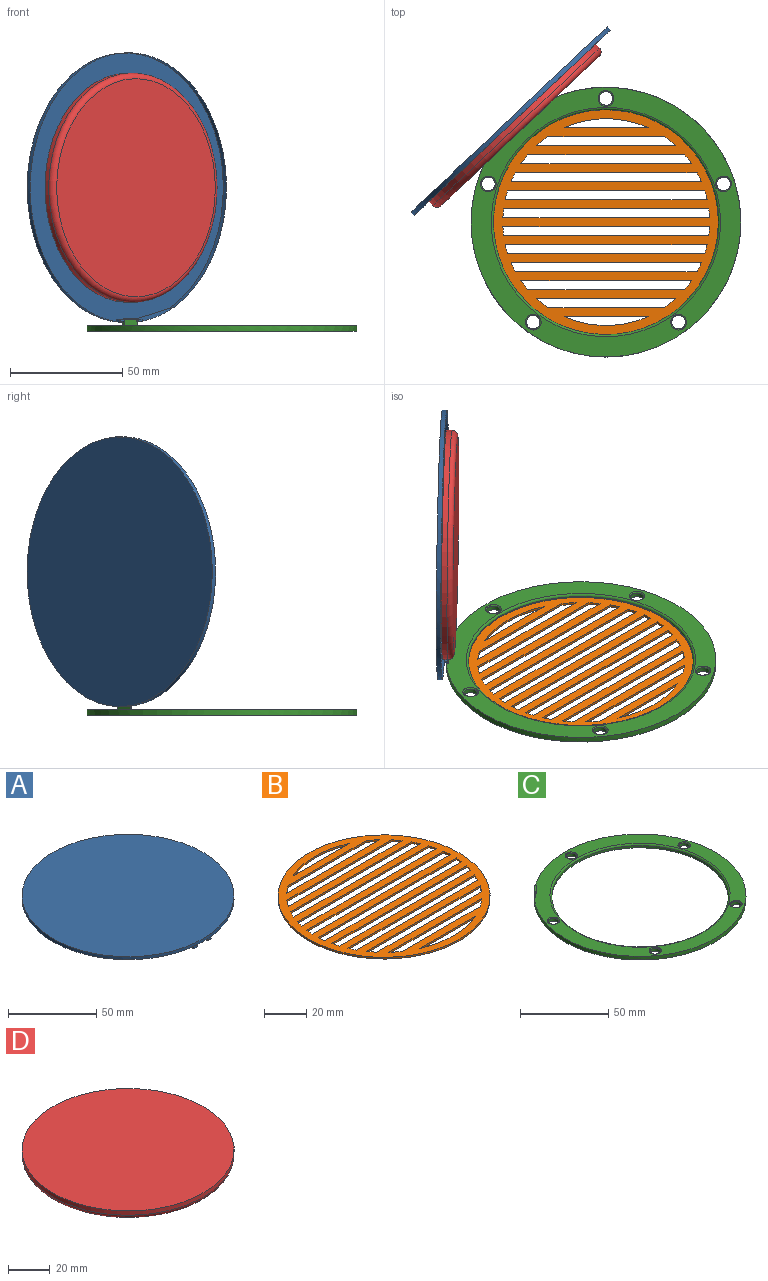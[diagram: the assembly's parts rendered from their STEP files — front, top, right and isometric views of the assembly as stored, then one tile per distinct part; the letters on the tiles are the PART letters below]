
ASSEMBLY  parts=4 mates=3
PART A: 21 faces, bbox 120x120x4 mm
  f0: plane 3x1.5mm, normal (0,1,0), area 4.5mm2, adj f4,f8,f10,f18
  f1: plane 3x1.5mm, normal (0,-1,0), area 4.5mm2, adj f4,f8,f10,f18
  f2: cylinder r=60mm len=120mm, axis (0,0,-1), area 754mm2, adj f3,f4
  f3: plane 120x120mm, normal (0,0,1), area 11309.7mm2, adj f2
  f4: plane 120x120mm, normal (0,0,-1), area 11303.7mm2, adj f0,f1,f2,f5,f6,f7,f8,f9
  f5: plane 3x1.5mm, normal (0,-1,0), area 4.5mm2, adj f4,f6,f9,f15
  f6: plane 1.5x1mm, normal (-1,0,0), area 1.5mm2, adj f4,f5,f7,f17
  f7: plane 3x1.5mm, normal (0,1,0), area 4.5mm2, adj f4,f6,f9,f15
  f8: plane 1.5x1mm, normal (1,0,0), area 1.5mm2, adj f0,f1,f4,f20
  f9: plane 1.5x1mm, normal (1,0,0), area 1.1mm2, adj f4,f5,f7,f13,f16
  f10: plane 1.5x1mm, normal (-1,0,0), area 1.1mm2, adj f0,f1,f4,f11,f19
  f11: cylinder r=0.35mm len=0.7mm, axis (1,0,0), area 0.6mm2, adj f10,f12,f19
  f12: plane 0.7x0.7mm, normal (-1,0,0), area 0.4mm2, adj f11
  f13: cylinder r=0.35mm len=0.7mm, axis (1,0,0), area 0.6mm2, adj f9,f14,f16
  f14: plane 0.7x0.7mm, normal (1,0,0), area 0.4mm2, adj f13
  f15: cylinder r=0.5mm len=3mm, axis (1,0,0), area 4.1mm2, adj f5,f7,f16,f17
  f16: cylinder r=0.5mm len=1mm, axis (0,-1,0), area 0.5mm2, adj f9,f13,f15
  f17: cylinder r=0.5mm len=1mm, axis (0,-1,0), area 0.5mm2, adj f6,f15
  f18: cylinder r=0.5mm len=3mm, axis (-1,0,0), area 4.1mm2, adj f0,f1,f19,f20
  f19: cylinder r=0.5mm len=1mm, axis (0,1,0), area 0.5mm2, adj f10,f11,f18
  f20: cylinder r=0.5mm len=1mm, axis (0,1,0), area 0.5mm2, adj f8,f18
PART B: 47 faces, bbox 100x100x1 mm
  f0: cylinder r=46mm len=37.52mm, axis (0,0,1), area 38.7mm2, adj f11,f12,f24
  f1: cylinder r=46mm len=5.06mm, axis (0,0,1), area 6.5mm2, adj f11,f12,f21,f23
  f2: cylinder r=46mm len=4mm, axis (0,0,1), area 5mm2, adj f11,f12,f19,f22
  f3: cylinder r=46mm len=5.06mm, axis (0,0,1), area 6.5mm2, adj f11,f12,f21,f23
  f4: cylinder r=46mm len=4mm, axis (0,0,1), area 4.4mm2, adj f11,f12,f17,f20
  f5: cylinder r=46mm len=4mm, axis (0,0,1), area 5mm2, adj f11,f12,f19,f22
  f6: cylinder r=46mm len=4mm, axis (0,0,1), area 4.1mm2, adj f11,f12,f15,f18
  f7: cylinder r=46mm len=4mm, axis (0,0,1), area 4.4mm2, adj f11,f12,f17,f20
  f8: cylinder r=46mm len=4mm, axis (0,0,1), area 4mm2, adj f11,f12,f14,f16
  f9: cylinder r=46mm len=4mm, axis (0,0,1), area 4.1mm2, adj f11,f12,f15,f18
  f10: cylinder r=50mm len=100mm, axis (0,0,-1), area 314.2mm2, adj f11,f12
  f11: plane 100x100mm, normal (0,0,1), area 4505.7mm2, adj f0,f1,f2,f3,f4,f5,f6,f7
  f12: plane 100x100mm, normal (0,0,-1), area 4505.7mm2, adj f0,f1,f2,f3,f4,f5,f6,f7
  f13: cylinder r=46mm len=4mm, axis (0,0,1), area 4mm2, adj f11,f12,f14,f16
  f14: plane 91.91x1mm, normal (0,1,0), area 91.9mm2, adj f8,f11,f12,f13
  f15: plane 89.8x1mm, normal (0,1,0), area 89.8mm2, adj f6,f9,f11,f12
  f16: plane 91.21x1mm, normal (0,-1,0), area 91.2mm2, adj f8,f11,f12,f13
  f17: plane 84.66x1mm, normal (0,1,0), area 84.7mm2, adj f4,f7,f11,f12
  f18: plane 87.64x1mm, normal (0,-1,0), area 87.6mm2, adj f6,f9,f11,f12
  f19: plane 75.89x1mm, normal (0,1,0), area 75.9mm2, adj f2,f5,f11,f12
  f20: plane 80.8x1mm, normal (0,-1,0), area 80.8mm2, adj f4,f7,f11,f12
  f21: plane 61.97x1mm, normal (0,1,0), area 62mm2, adj f1,f3,f11,f12
  f22: plane 69.74x1mm, normal (0,-1,0), area 69.7mm2, adj f2,f5,f11,f12
  f23: plane 51.85x1mm, normal (0,-1,0), area 51.8mm2, adj f1,f3,f11,f12
  f24: plane 37.52x1mm, normal (0,1,0), area 37.5mm2, adj f0,f11,f12
  f25: cylinder r=46mm len=37.52mm, axis (0,0,1), area 38.7mm2, adj f11,f12,f46
  f26: cylinder r=46mm len=5.06mm, axis (0,0,1), area 6.5mm2, adj f11,f12,f43,f45
  f27: cylinder r=46mm len=4mm, axis (0,0,1), area 5mm2, adj f11,f12,f41,f44
  f28: cylinder r=46mm len=5.06mm, axis (0,0,1), area 6.5mm2, adj f11,f12,f43,f45
  f29: cylinder r=46mm len=4mm, axis (0,0,1), area 4.4mm2, adj f11,f12,f39,f42
  f30: cylinder r=46mm len=4mm, axis (0,0,1), area 5mm2, adj f11,f12,f41,f44
  f31: cylinder r=46mm len=4mm, axis (0,0,1), area 4.1mm2, adj f11,f12,f37,f40
  f32: cylinder r=46mm len=4mm, axis (0,0,1), area 4.4mm2, adj f11,f12,f39,f42
  f33: cylinder r=46mm len=4mm, axis (0,0,1), area 4mm2, adj f11,f12,f36,f38
  f34: cylinder r=46mm len=4mm, axis (0,0,1), area 4.1mm2, adj f11,f12,f37,f40
  f35: cylinder r=46mm len=4mm, axis (0,0,1), area 4mm2, adj f11,f12,f36,f38
  f36: plane 91.91x1mm, normal (0,-1,0), area 91.9mm2, adj f11,f12,f33,f35
  f37: plane 89.8x1mm, normal (0,-1,0), area 89.8mm2, adj f11,f12,f31,f34
  f38: plane 91.21x1mm, normal (0,1,0), area 91.2mm2, adj f11,f12,f33,f35
  f39: plane 84.66x1mm, normal (0,-1,0), area 84.7mm2, adj f11,f12,f29,f32
  f40: plane 87.64x1mm, normal (0,1,0), area 87.6mm2, adj f11,f12,f31,f34
  f41: plane 75.89x1mm, normal (0,-1,0), area 75.9mm2, adj f11,f12,f27,f30
  f42: plane 80.8x1mm, normal (0,1,0), area 80.8mm2, adj f11,f12,f29,f32
  f43: plane 61.97x1mm, normal (0,-1,0), area 62mm2, adj f11,f12,f26,f28
  f44: plane 69.74x1mm, normal (0,1,0), area 69.7mm2, adj f11,f12,f27,f30
  f45: plane 51.85x1mm, normal (0,1,0), area 51.8mm2, adj f11,f12,f26,f28
  f46: plane 37.52x1mm, normal (0,-1,0), area 37.5mm2, adj f11,f12,f25
PART C: 22 faces, bbox 120x120x5.5 mm
  f0: plane 5.82x5.49mm, normal (0,0,1), area 0.7mm2, adj f2,f10
  f1: plane 120x120mm, normal (0,0,1), area 2937.3mm2, adj f2,f11,f12,f13,f15,f16,f17,f18
  f2: cylinder r=60mm len=120mm, axis (0,0,-1), area 942.5mm2, adj f0,f1,f3
  f3: plane 120x120mm, normal (0,0,-1), area 3314.4mm2, adj f2,f4,f5,f6,f7,f8,f9
  f4: cylinder r=50mm len=100mm, axis (0,0,1), area 471.2mm2, adj f3,f15
  f5: cylinder r=3mm len=6mm, axis (0,0,1), area 37.7mm2, adj f3,f20
  f6: cylinder r=3mm len=6mm, axis (0,0,1), area 37.7mm2, adj f3,f19
  f7: cylinder r=3mm len=6mm, axis (0,0,1), area 37.7mm2, adj f3,f18
  f8: cylinder r=3mm len=6mm, axis (0,0,1), area 37.7mm2, adj f3,f17
  f9: cylinder r=3mm len=6mm, axis (0,0,1), area 37.7mm2, adj f3,f16
  f10: plane 5.82x5.49mm, normal (-0.69,0.73,0), area 20mm2, adj f0,f11,f13,f21
  f11: plane 3x0.73mm, normal (-0.73,-0.69,0), area 2.4mm2, adj f1,f10,f12,f14,f21
  f12: plane 5.82x5.49mm, normal (0.69,-0.73,0), area 20mm2, adj f1,f11,f13,f21
  f13: plane 3x0.73mm, normal (0.73,0.69,0), area 2.4mm2, adj f1,f10,f12,f14,f21
  f14: cylinder r=0.4mm len=6.36mm, axis (-0.73,-0.69,0), area 20.1mm2, adj f11,f13
  f15: torus R=51mm, axis (0,0,1), area 497.1mm2, adj f1,f4
  f16: torus R=3.5mm, axis (0,0,1), area 15.7mm2, adj f1,f9
  f17: torus R=3.5mm, axis (0,0,1), area 15.7mm2, adj f1,f8
  f18: torus R=3.5mm, axis (0,0,1), area 15.7mm2, adj f1,f7
  f19: torus R=3.5mm, axis (0,0,1), area 15.7mm2, adj f1,f6
  f20: torus R=3.5mm, axis (0,0,1), area 15.7mm2, adj f1,f5
  f21: cylinder r=0.5mm len=6.5mm, axis (0.73,0.69,0), area 12.6mm2, adj f10,f11,f12,f13
PART D: 4 faces, bbox 110.4x110.4x5 mm
  f0: cylinder r=51mm len=102mm, axis (0,0,-1), area 801.1mm2, adj f1,f3
  f1: plane 102x102mm, normal (0,0,1), area 8171.3mm2, adj f0
  f2: plane 97x97mm, normal (0,0,-1), area 7389.8mm2, adj f3
  f3: torus R=48.5mm, axis (0,0,1), area 1236mm2, adj f0,f2
PLACE A rot(axis=(0.27,-0.68,-0.68),149.7deg) t=(-47.06,50.04,65.81)mm
PLACE B rot(axis=(1,0,0),180deg) t=(-5.3,5.98,3.02)mm
PLACE C t=(-5.43,5.98,2.02)mm
PLACE D rot(axis=(-0.87,-0.35,0.35),97.8deg) t=(-43.63,46.4,65.81)mm
MATE fastened D.f0 <-> A.f2  axis (-0.69,0.73,0) through (-47.06,50.04,65.81)mm
MATE fastened C.f4 <-> B.f10  axis (0,0,-1) through (-5.43,5.98,2.02)mm
MATE revolute A.f11 <-> C.f14  axis (-0.73,-0.69,0) through (-43.29,51.88,6.72)mm
